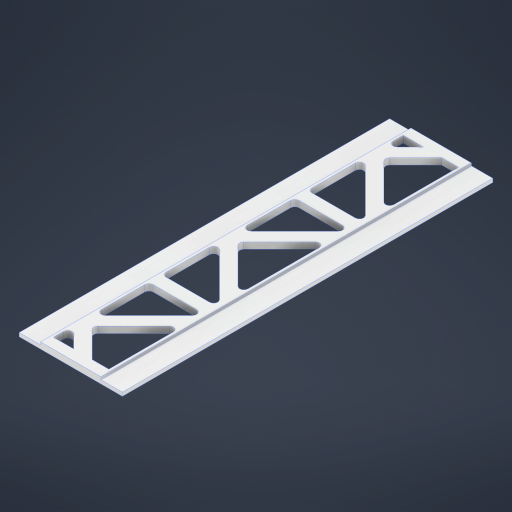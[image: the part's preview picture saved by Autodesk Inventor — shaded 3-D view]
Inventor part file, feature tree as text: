
AUTODESK INVENTOR PART (.ipt)
format: ipt  version: 2024 (Build 280153000, 153)  size: 396,288 bytes
history: native  units: mm
features: extrude x6, sketch x6, projected_geometry x2, other x1, fillet x1
ambient origin geometry x8: Origin, YZ Plane, XZ Plane, XY Plane, X Axis, Y Axis, Z Axis, Center Point
bodies: Body1 (feature_tree)
feature tree (16):
  other  "Твердое тело1"
  extrude  "Выдавливание1"  Depth=140.0mm
  extrude  "Выдавливание2"  Depth=12.0mm
  extrude  "Выдавливание4"  Depth=5.0mm TaperAngle=0.0deg
  extrude  "Extrusion6"  Depth=5.0mm
  fillet  "Fillet2"  [1 undecoded]
  extrude  "Extrusion7"  TaperAngle=90.0deg  [1 undecoded]
  extrude  "Extrusion8"  TaperAngle=90.0deg  [1 undecoded]
  sketch  "Эскиз1"
  sketch  "Эскиз2"
  projected_geometry  "Спроецированная петля1"
  sketch  "Эскиз3"
  projected_geometry  "Спроецированная петля2"
  sketch  "Sketch5"  dims[d0=777.0mm d1=140.0mm]
  sketch  "Sketch6"  dims[d2=12.0mm d3=0.0mm d4=12.0mm]
  sketch  "Sketch7"  dims[d5=12.0mm d6=5.0mm d7=0.0mm d8=5.0mm d11=90.0deg d12=90.0deg d13=90.0deg d15=90.0deg d16=90.0deg d17=108.5mm d18=45.0deg d22=25.0mm d25=23.0mm d26=0.0mm d34=25.0mm d35=25.0mm d38=23.0mm d39=0.0mm d40=8.0mm d41=41.0mm d42=41.0mm d43=33.0mm d44=33.0mm d45=30.0mm d46=0.0mm d47=20.0mm d48=20.0mm d49=30.0mm d50=0.0mm d30=0.5mm d31=0.872665mm d32=0.5mm d33=0.872665mm]
note: 3 required parameter values undecoded (feature->parameter linkage not recoverable at this tier; creation-order binding heuristic only, values carry confidence <= 0.55)
